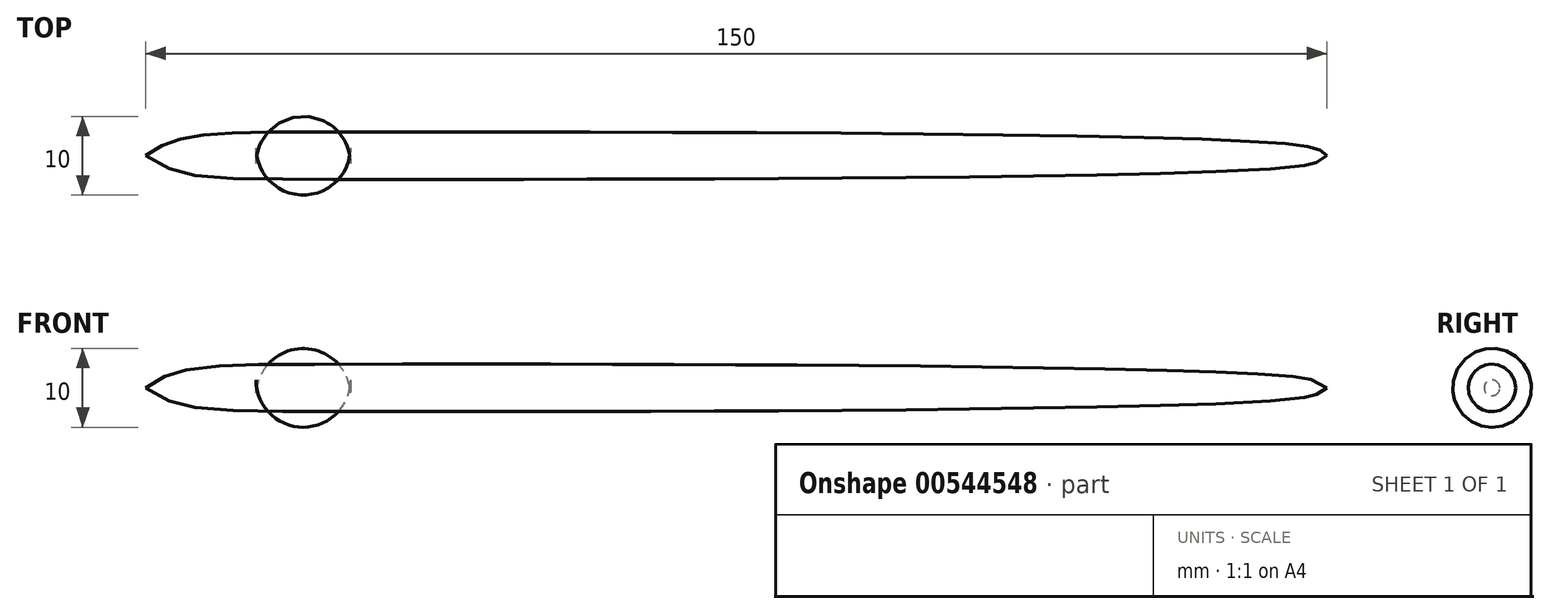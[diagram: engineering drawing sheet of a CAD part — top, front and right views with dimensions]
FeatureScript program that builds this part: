
annotation { "Feature Type Name" : "Feature", "Feature Type Description" : "" }
export const myFeature = defineFeature(function(context is Context, id is Id, definition is map)
    precondition{}
    {
        {
            var Q0;
            Q0=qCreatedBy(makeId("Top.planeOp"),FACE);
            var sketch = newSketch(context, id + "F0", { "sketchPlane" : qUnion([Q0])});
            skLineSegment(sketch, "E0", {"start": v(0, 0) * mm, "end": v(150, 0) * mm});
            skLineSegment(sketch, "E1", {"start": v(0, 0) * mm, "end": v(20, 3) * mm, "construction": true});
            skLineSegment(sketch, "E2", {"start": v(20, 3) * mm, "end": v(145, 1.5) * mm, "construction": true});
            skLineSegment(sketch, "E3", {"start": v(145, 1.5) * mm, "end": v(150, 0) * mm, "construction": true});
            skFitSpline(sketch, "E4", {"points": [v(0, 0) * mm, v(20, 3) * mm, v(145, 1.5) * mm, v(150, 0) * mm], "startDerivative": vector(45.7, 35.14) * mm, "endDerivative": vector(17.1, -18.99) * mm});
            skSolve(sketch);
        }
        {
            var Q0;
            Q0=makeQuery(id+"F0.imprint","IMPRINT",FACE,{"disambiguationData":[TD([[makeQuery(id+"F0.imprint","IMPRINT",EDGE,{"derivedFrom":sQuery(id+"F0.wireOp",EDGE,"E0")}),1.0]])]});
            var Q1;
            Q1=sQuery(id+"F0.wireOp",EDGE,"E0");
            revolve(context, id + "F1", {"entities" : qUnion([Q0]), "axis" : qUnion([Q1]), "revolveType" : RevolveType.FULL});
        }
        {
            var Q0;
            Q0=qCreatedBy(makeId("Top.planeOp"),FACE);
            var sketch = newSketch(context, id + "F2", { "sketchPlane" : qUnion([Q0])});
            skLineSegment(sketch, "E5.bottom", {"start": v(14, 0) * mm, "end": v(26, 0) * mm});
            skLineSegment(sketch, "E5.top", {"start": v(14, 1) * mm, "end": v(26, 1) * mm, "construction": true});
            skLineSegment(sketch, "E5.left", {"start": v(14, 0) * mm, "end": v(14, 1) * mm});
            skLineSegment(sketch, "E5.right", {"start": v(26, 0) * mm, "end": v(26, 1) * mm});
            skArc(sketch, "E6", {"start": v(26, 1) * mm, "mid": v(20, 7) * mm, "end": v(14, 1) * mm});
            skSolve(sketch);
        }
        {
            var Q0;
            Q0=makeQuery(id+"F2.imprint","IMPRINT",FACE,{"disambiguationData":[TD([[makeQuery(id+"F2.imprint","IMPRINT",EDGE,{"derivedFrom":sQuery(id+"F2.wireOp",EDGE,"E5.bottom")}),1.0]])]});
            var Q1;
            Q1=sQuery(id+"F2.wireOp",EDGE,"E5.bottom");
            revolve(context, id + "F3", {"entities" : qUnion([Q0]), "axis" : qUnion([Q1]), "revolveType" : RevolveType.FULL});
        }
    });
